AUTODESK INVENTOR PART (.ipt)
format: ipt  version: 2021 (Build 250183000, 183)  size: 132,608 bytes
history: native  units: mm
features: other x7, extrude x2, sketch x2, reference x2, fillet x1, chamfer x1, projected_geometry x1
ambient origin geometry x8: Origin, YZ Plane, XZ Plane, XY Plane, X Axis, Y Axis, Z Axis, Center Point
bodies: Body1 (feature_tree)
feature tree (16):
  other  "Bryła1"
  other  "Płaszczyzna konstrukcyjna1"
  other  "Płaszczyzna konstrukcyjna2"
  extrude  "Wyciągnięcie proste1"  Depth=16.0mm
  fillet  "Zaokrąglenie1"  Radius=48.0mm
  extrude  "Wyciągnięcie proste2"  Depth=7.0mm
  chamfer  "Faza1"  Distance=30.0mm
  sketch  "Szkic1"
  sketch  "Szkic2"
  projected_geometry  "Pętla rzutowana1"
  reference  "Odniesienie1"
  reference  "Odniesienie2"
  other  "wszystko.iam"
  other  "trmometr:1"
  other  "bolec:1"
  other  "fiolka:1"
